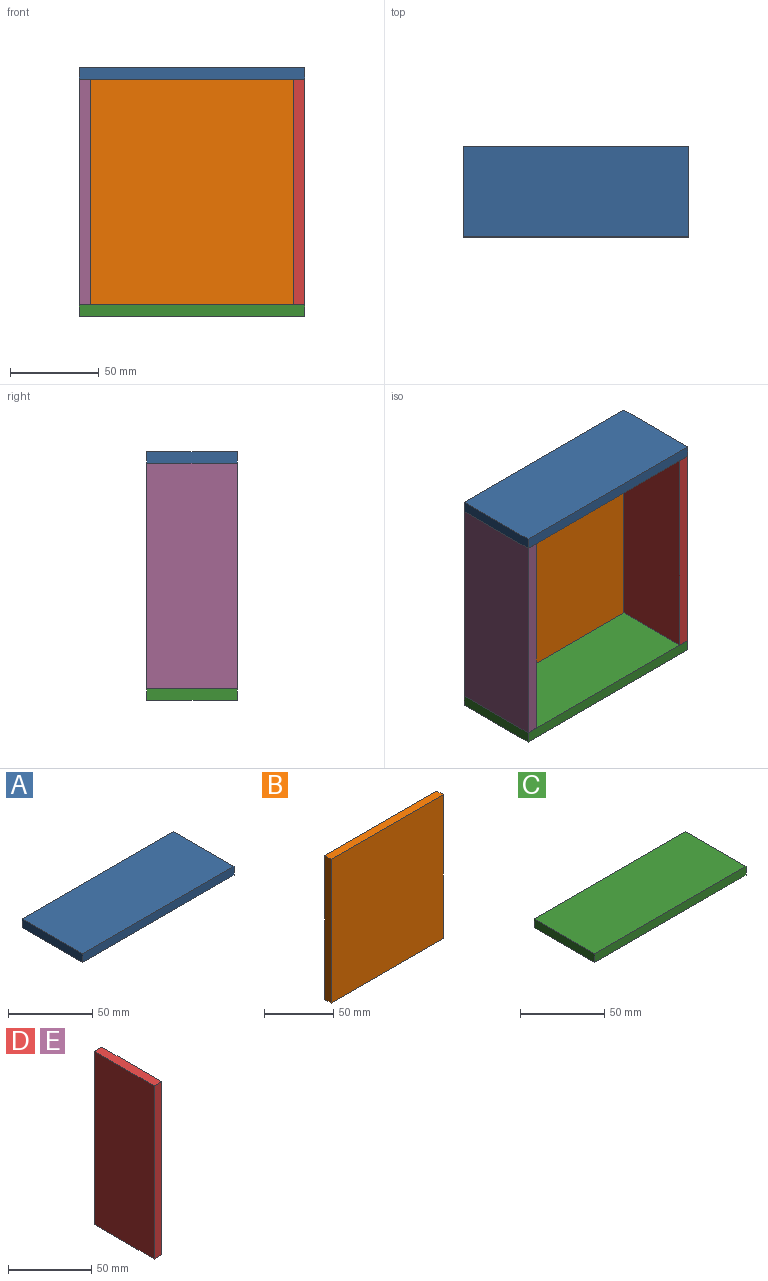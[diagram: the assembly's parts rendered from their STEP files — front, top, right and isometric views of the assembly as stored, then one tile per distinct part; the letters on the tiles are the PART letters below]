
ASSEMBLY  parts=5 mates=12
PART A: 6 faces, bbox 127x50.8x6.4 mm
  f0: plane 127x6.35mm, normal (0,1,0), area 806.5mm2, adj f1,f3,f4,f5
  f1: plane 50.8x6.35mm, normal (-1,0,0), area 322.6mm2, adj f0,f2,f4,f5
  f2: plane 127x6.35mm, normal (0,-1,0), area 806.5mm2, adj f1,f3,f4,f5
  f3: plane 50.8x6.35mm, normal (1,0,0), area 322.6mm2, adj f0,f2,f4,f5
  f4: plane 127x50.8mm, normal (0,0,1), area 6451.6mm2, adj f0,f1,f2,f3
  f5: plane 127x50.8mm, normal (0,0,-1), area 6451.6mm2, adj f0,f1,f2,f3
PART B: 6 faces, bbox 114.3x6.4x127 mm
  f0: plane 114.3x6.35mm, normal (0,0,1), area 725.8mm2, adj f2,f3,f4,f5
  f1: plane 114.3x6.35mm, normal (0,0,-1), area 725.8mm2, adj f2,f3,f4,f5
  f2: plane 127x6.35mm, normal (-1,0,0), area 806.5mm2, adj f0,f1,f3,f4
  f3: plane 127x114.3mm, normal (0,-1,0), area 14516.1mm2, adj f0,f1,f2,f5
  f4: plane 127x114.3mm, normal (0,1,0), area 14516.1mm2, adj f0,f1,f2,f5
  f5: plane 127x6.35mm, normal (1,0,0), area 806.5mm2, adj f0,f1,f3,f4
PART C: 6 faces, bbox 127x50.8x6.4 mm
  f0: plane 127x6.35mm, normal (0,1,0), area 806.5mm2, adj f1,f3,f4,f5
  f1: plane 50.8x6.35mm, normal (-1,0,0), area 322.6mm2, adj f0,f2,f4,f5
  f2: plane 127x6.35mm, normal (0,-1,0), area 806.5mm2, adj f1,f3,f4,f5
  f3: plane 50.8x6.35mm, normal (1,0,0), area 322.6mm2, adj f0,f2,f4,f5
  f4: plane 127x50.8mm, normal (0,0,1), area 6451.6mm2, adj f0,f1,f2,f3
  f5: plane 127x50.8mm, normal (0,0,-1), area 6451.6mm2, adj f0,f1,f2,f3
PART D: 6 faces, bbox 6.4x50.8x127 mm
  f0: plane 127x6.35mm, normal (0,1,0), area 806.5mm2, adj f1,f3,f4,f5
  f1: plane 50.8x6.35mm, normal (0,0,1), area 322.6mm2, adj f0,f2,f4,f5
  f2: plane 127x6.35mm, normal (0,-1,0), area 806.5mm2, adj f1,f3,f4,f5
  f3: plane 50.8x6.35mm, normal (0,0,-1), area 322.6mm2, adj f0,f2,f4,f5
  f4: plane 127x50.8mm, normal (1,0,0), area 6451.6mm2, adj f0,f1,f2,f3
  f5: plane 127x50.8mm, normal (-1,0,0), area 6451.6mm2, adj f0,f1,f2,f3
PART E: same geometry as D
PLACE A t=(32.22,-2.43,166.71)mm
PLACE B t=(-22.52,19.04,44.13)mm
PLACE C t=(-82.78,19.04,33.36)mm
PLACE D t=(-22.52,-23.36,39.71)mm
PLACE E t=(-143.17,-23.36,39.71)mm
MATE planar D.f2 <-> C.f2  axis (0,-1,0) through (-19.34,-31.76,103.21)mm
MATE planar A.f0 <-> B.f4  axis (0,1,0) through (-79.67,19.04,169.89)mm
MATE planar A.f5 <-> B.f0  axis (0,0,-1) through (-79.67,-6.36,166.71)mm
MATE planar B.f4 <-> C.f0  axis (0,1,0) through (-79.67,19.04,103.21)mm
MATE planar E.f3 <-> C.f4  axis (0,0,-1) through (-139.99,-6.36,39.71)mm
MATE planar B.f1 <-> C.f4  axis (0,0,-1) through (-79.67,15.87,39.71)mm
MATE planar D.f4 <-> C.f3  axis (1,0,0) through (-16.17,-6.36,103.21)mm
MATE planar D.f3 <-> C.f4  axis (0,0,-1) through (-19.34,-6.36,39.71)mm
MATE planar E.f0 <-> C.f0  axis (0,1,0) through (-139.99,19.04,103.21)mm
MATE planar A.f1 <-> E.f5  axis (-1,0,0) through (-143.17,-6.36,166.71)mm
MATE planar B.f5 <-> D.f5  axis (1,0,0) through (-22.52,15.87,103.21)mm
MATE planar E.f5 <-> C.f1  axis (-1,0,0) through (-143.17,-6.36,103.21)mm
